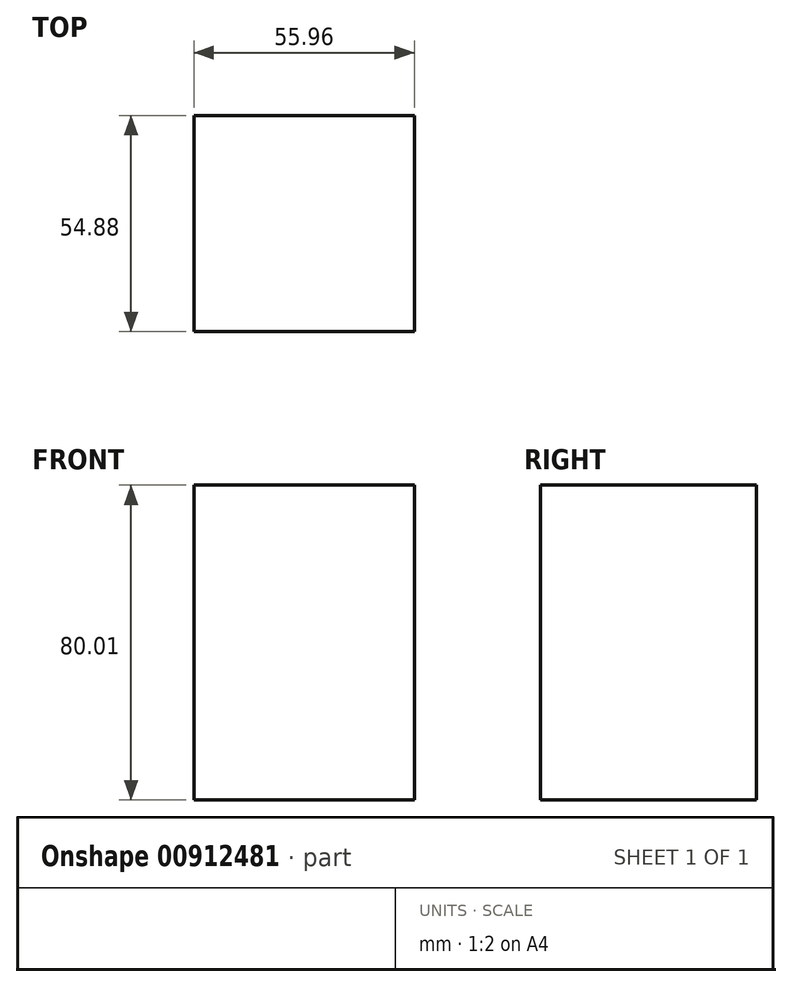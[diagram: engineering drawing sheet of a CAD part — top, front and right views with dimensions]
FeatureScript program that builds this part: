
annotation { "Feature Type Name" : "Feature", "Feature Type Description" : "" }
export const myFeature = defineFeature(function(context is Context, id is Id, definition is map)
    precondition{}
    {
        {
            var Q0;
            Q0=qCreatedBy(makeId("Top.planeOp"),FACE);
            var sketch = newSketch(context, id + "F0", { "sketchPlane" : qUnion([Q0])});
            skLineSegment(sketch, "E0.bottom", {"start": v(27.98, -27.44) * mm, "end": v(-27.98, -27.44) * mm});
            skLineSegment(sketch, "E0.top", {"start": v(27.98, 27.44) * mm, "end": v(-27.98, 27.44) * mm});
            skLineSegment(sketch, "E0.left", {"start": v(27.98, -27.44) * mm, "end": v(27.98, 27.44) * mm});
            skLineSegment(sketch, "E0.right", {"start": v(-27.98, -27.44) * mm, "end": v(-27.98, 27.44) * mm});
            skPoint(sketch, "E0.middle", {"position": v(0, 0) * mm});
            skSolve(sketch);
        }
        {
            var Q0;
            Q0 = qSketchRegion(id + "F0", true);
            extrude(context, id + "F1", {"entities" : qUnion([Q0]), "depth" : 80 * mm, "offsetDistance" : 25.4 * mm});
        }
    });
